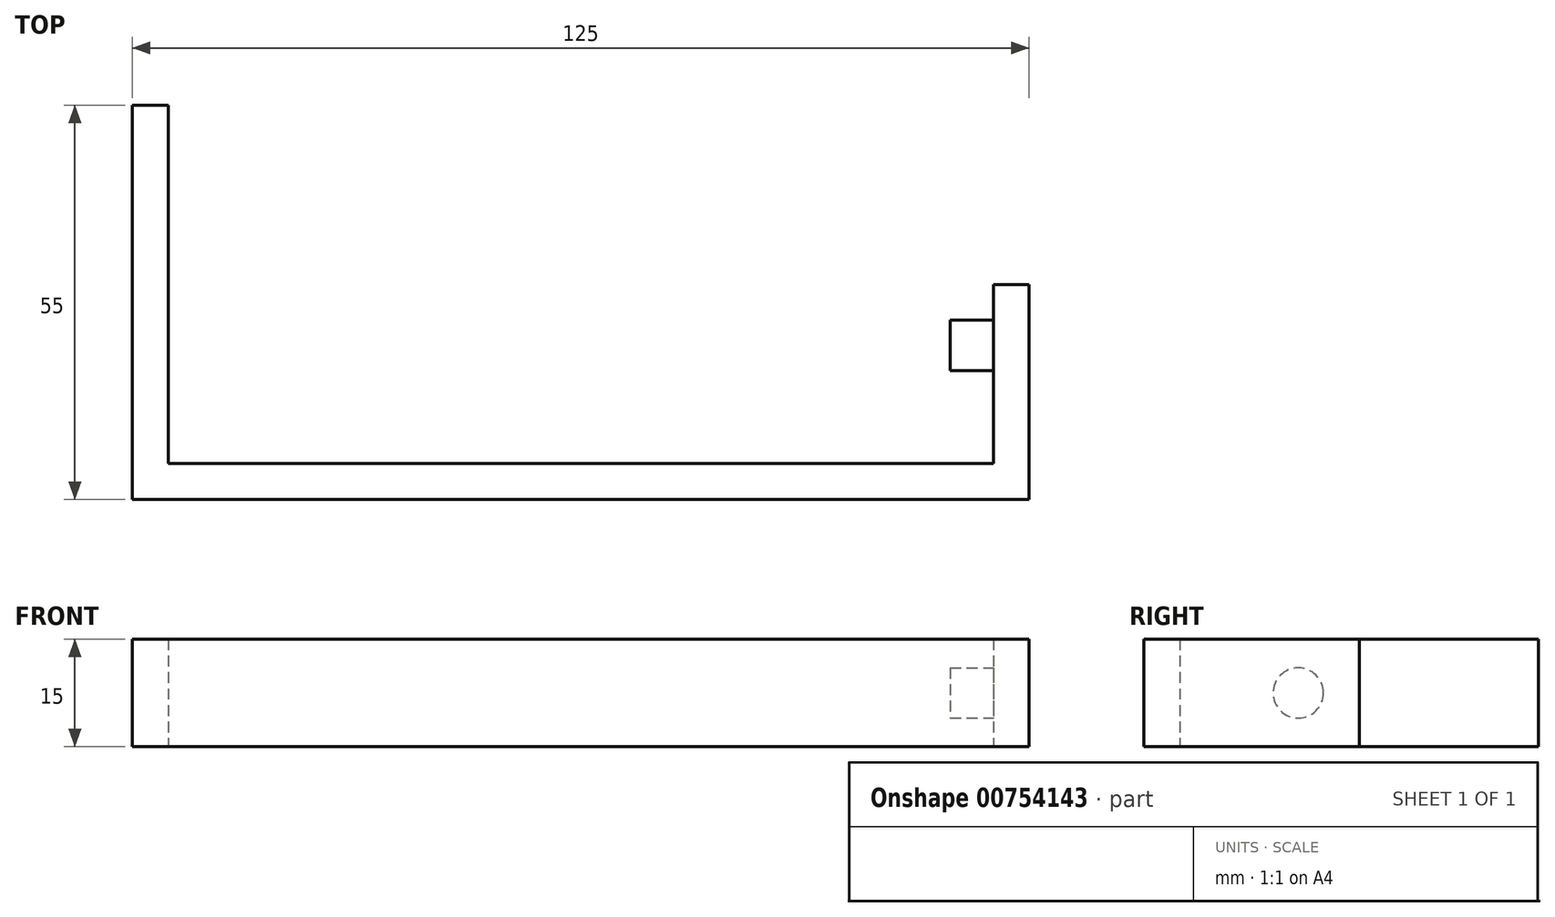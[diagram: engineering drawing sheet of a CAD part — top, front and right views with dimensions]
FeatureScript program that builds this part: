
annotation { "Feature Type Name" : "Feature", "Feature Type Description" : "" }
export const myFeature = defineFeature(function(context is Context, id is Id, definition is map)
    precondition{}
    {
        {
            var Q0;
            Q0=qCreatedBy(makeId("Top.planeOp"),FACE);
            var sketch = newSketch(context, id + "F0", { "sketchPlane" : qUnion([Q0])});
            skLineSegment(sketch, "E0", {"start": v(-171.38, 166.58) * mm, "end": v(-171.38, 111.58) * mm});
            skLineSegment(sketch, "E1", {"start": v(-171.38, 111.58) * mm, "end": v(-46.38, 111.58) * mm});
            skLineSegment(sketch, "E2", {"start": v(-46.38, 111.58) * mm, "end": v(-46.38, 141.58) * mm});
            skLineSegment(sketch, "E3", {"start": v(-171.38, 166.58) * mm, "end": v(-166.38, 166.58) * mm});
            skLineSegment(sketch, "E4", {"start": v(-166.38, 166.58) * mm, "end": v(-166.38, 116.58) * mm});
            skLineSegment(sketch, "E5", {"start": v(-166.38, 116.58) * mm, "end": v(-51.38, 116.58) * mm});
            skLineSegment(sketch, "E6", {"start": v(-51.38, 116.58) * mm, "end": v(-51.38, 141.58) * mm});
            skLineSegment(sketch, "E7", {"start": v(-51.38, 141.58) * mm, "end": v(-46.38, 141.58) * mm});
            skSolve(sketch);
        }
        {
            var Q0;
            Q0=makeQuery(id+"F0.imprint","IMPRINT",FACE,{"disambiguationData":[TD([[makeQuery(id+"F0.imprint","IMPRINT",EDGE,{"derivedFrom":sQuery(id+"F0.wireOp",EDGE,"E0")}),1.0]])]});
            extrude(context, id + "F1", {"entities" : qUnion([Q0]), "depth" : 15 * mm, "offsetDistance" : 25 * mm});
        }
        {
            var Q0;
            Q0=makeQuery(id+"F1.opExtrude","SWEPT_FACE",FACE,{"disambiguationData":[OSD([sQuery(id+"F0.wireOp",EDGE,"E6")])]});
            var sketch = newSketch(context, id + "F2", { "sketchPlane" : qUnion([Q0])});
            skCircle(sketch, "E8", {"center": v(-133.08, 7.5) * mm, "radius": 3.5 * mm});
            skSolve(sketch);
        }
        {
            var Q0;
            Q0=makeQuery(id+"F2.imprint","IMPRINT",FACE,{"disambiguationData":[TD([[makeQuery(id+"F2.imprint","IMPRINT",EDGE,{"derivedFrom":sQuery(id+"F2.wireOp",EDGE,"E8")}),1.0]])]});
            extrude(context, id + "F3", {"entities" : qUnion([Q0]), "operationType" : NewBodyOperationType.ADD, "depth" : 6 * mm, "offsetDistance" : 25 * mm});
        }
    });
